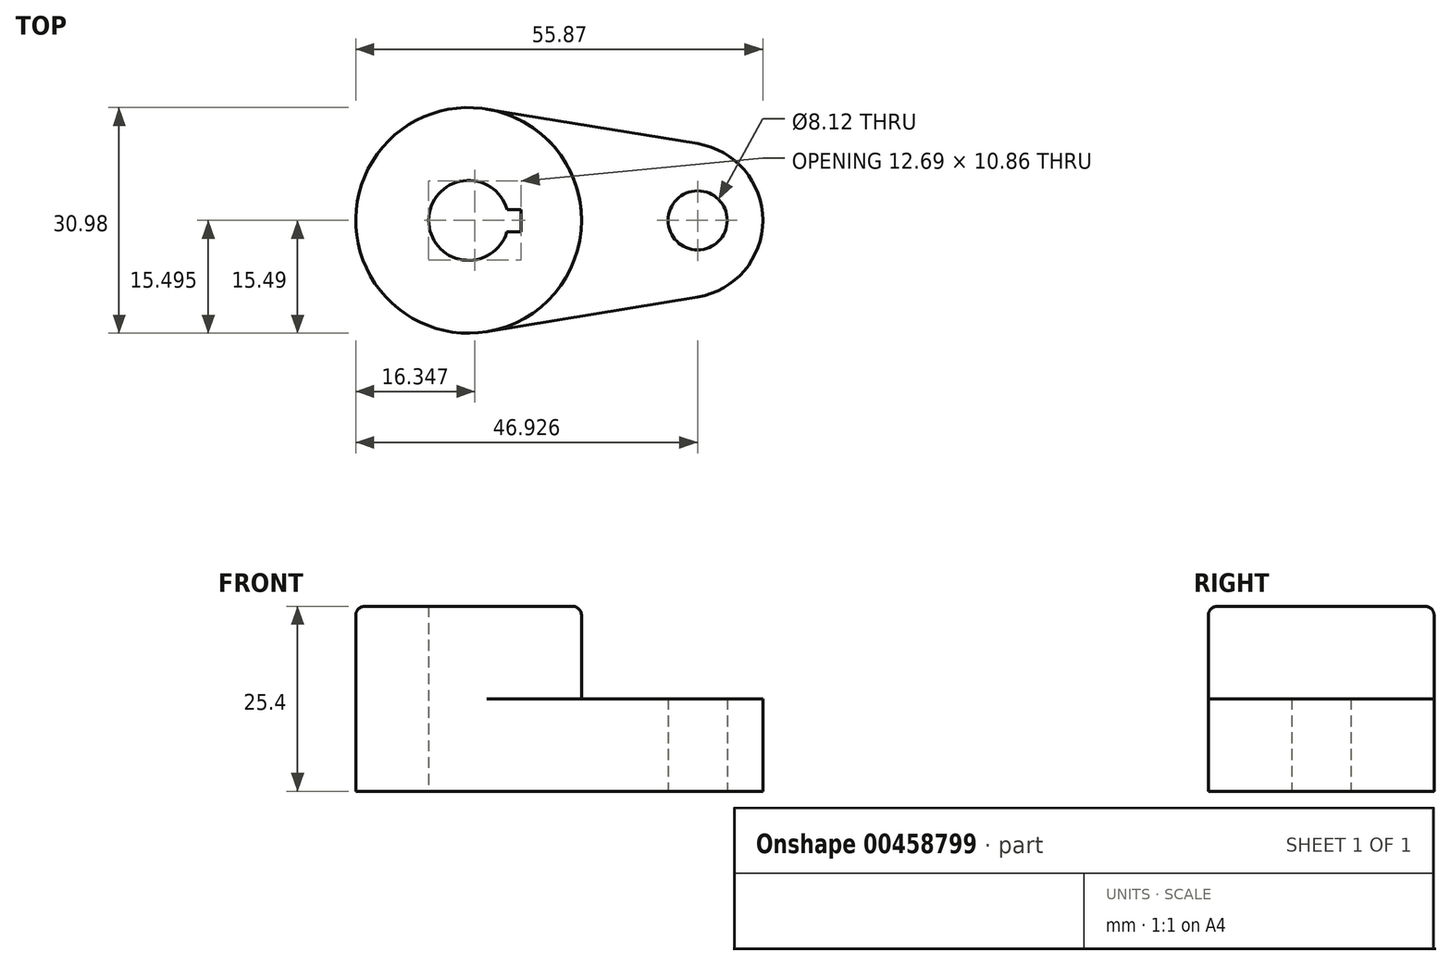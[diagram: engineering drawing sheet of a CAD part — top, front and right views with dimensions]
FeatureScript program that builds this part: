
annotation { "Feature Type Name" : "Feature", "Feature Type Description" : "" }
export const myFeature = defineFeature(function(context is Context, id is Id, definition is map)
    precondition{}
    {
        {
            var Q0;
            Q0=qCreatedBy(makeId("Top.planeOp"),FACE);
            var sketch = newSketch(context, id + "F0", { "sketchPlane" : qUnion([Q0])});
            skCircle(sketch, "E0", {"center": v(0, 0) * mm, "radius": 5.49 * mm});
            skCircle(sketch, "E1", {"center": v(0, 0) * mm, "radius": 15.49 * mm});
            skCircle(sketch, "E2", {"center": v(31.44, 0) * mm, "radius": 4.06 * mm});
            skLineSegment(sketch, "E3", {"start": v(31.44, 10.53) * mm, "end": v(2.51, 15.28) * mm});
            skLineSegment(sketch, "E4", {"start": v(31.44, -10.53) * mm, "end": v(2.51, -15.28) * mm});
            skLineSegment(sketch, "E5.bottom", {"start": v(-7.43, 1.5) * mm, "end": v(7.2, 1.5) * mm});
            skLineSegment(sketch, "E5.top", {"start": v(-7.43, -1.58) * mm, "end": v(7.2, -1.58) * mm});
            skLineSegment(sketch, "E5.left", {"start": v(-7.43, 1.5) * mm, "end": v(-7.43, -1.58) * mm});
            skLineSegment(sketch, "E5.right", {"start": v(7.2, 1.5) * mm, "end": v(7.2, -1.58) * mm});
            skArc(sketch, "E6", {"start": v(31.44, 10.53) * mm, "mid": v(40.38, 0) * mm, "end": v(31.44, -10.53) * mm});
            skSolve(sketch);
        }
        {
            var Q0;
            Q0=makeQuery(id+"F0.imprint","IMPRINT",FACE,{"disambiguationData":[TD([[makeQuery(id+"F0.imprint","IMPRINT",EDGE,{"derivedFrom":sQuery(id+"F0.wireOp",EDGE,"E2")}),-1.0]])]});
            var Q1;
            {var subQ0=sQuery(id+"F0.wireOp",EDGE,"E3");Q1=makeQuery(id+"F0.imprint","IMPRINT",FACE,{"disambiguationData":[TD([[makeQuery(id+"F0.imprint","IMPRINT",EDGE,{"derivedFrom":subQ0}),1.0]])]});}
            var Q2;
            {var subQ11=sQuery(id+"F0.wireOp",EDGE,"E5.left");Q2=makeQuery(id+"F0.imprint","IMPRINT",FACE,{"disambiguationData":[TD([[makeQuery(id+"F0.imprint","IMPRINT",EDGE,{"derivedFrom":subQ11}),-1.0]])]});}
            var Q3;
            {var subQ5=sQuery(id+"F0.wireOp",EDGE,"E5.left");Q3=makeQuery(id+"F0.imprint","IMPRINT",FACE,{"disambiguationData":[TD([[makeQuery(id+"F0.imprint","IMPRINT",EDGE,{"derivedFrom":subQ5}),1.0]])]});}
            extrude(context, id + "F1", {"entities" : qUnion([Q0, Q1, Q2, Q3]), "depth" : 12.7 * mm});
        }
        {
            var Q0;
            {var subQ11=sQuery(id+"F0.wireOp",EDGE,"E5.left");Q0=makeQuery(id+"F0.imprint","IMPRINT",FACE,{"disambiguationData":[TD([[makeQuery(id+"F0.imprint","IMPRINT",EDGE,{"derivedFrom":subQ11}),-1.0]])]});}
            var Q1;
            {var subQ5=sQuery(id+"F0.wireOp",EDGE,"E5.left");Q1=makeQuery(id+"F0.imprint","IMPRINT",FACE,{"disambiguationData":[TD([[makeQuery(id+"F0.imprint","IMPRINT",EDGE,{"derivedFrom":subQ5}),1.0]])]});}
            extrude(context, id + "F2", {"entities" : qUnion([Q0, Q1]), "operationType" : NewBodyOperationType.ADD, "depth" : 25.4 * mm});
        }
        {
            var Q0;
            Q0=makeQuery(id+"F2.opExtrude","CAP_EDGE",EDGE,{"disambiguationData":[OSD([sQuery(id+"F0.wireOp",EDGE,"E1")])],"isStart":false});
            fillet(context, id + "F3", {"entities" : qUnion([Q0]), "radius" : 1.23 * mm, "tangentPropagation" : true, "allowEdgeOverflow" : false});
        }
    });
